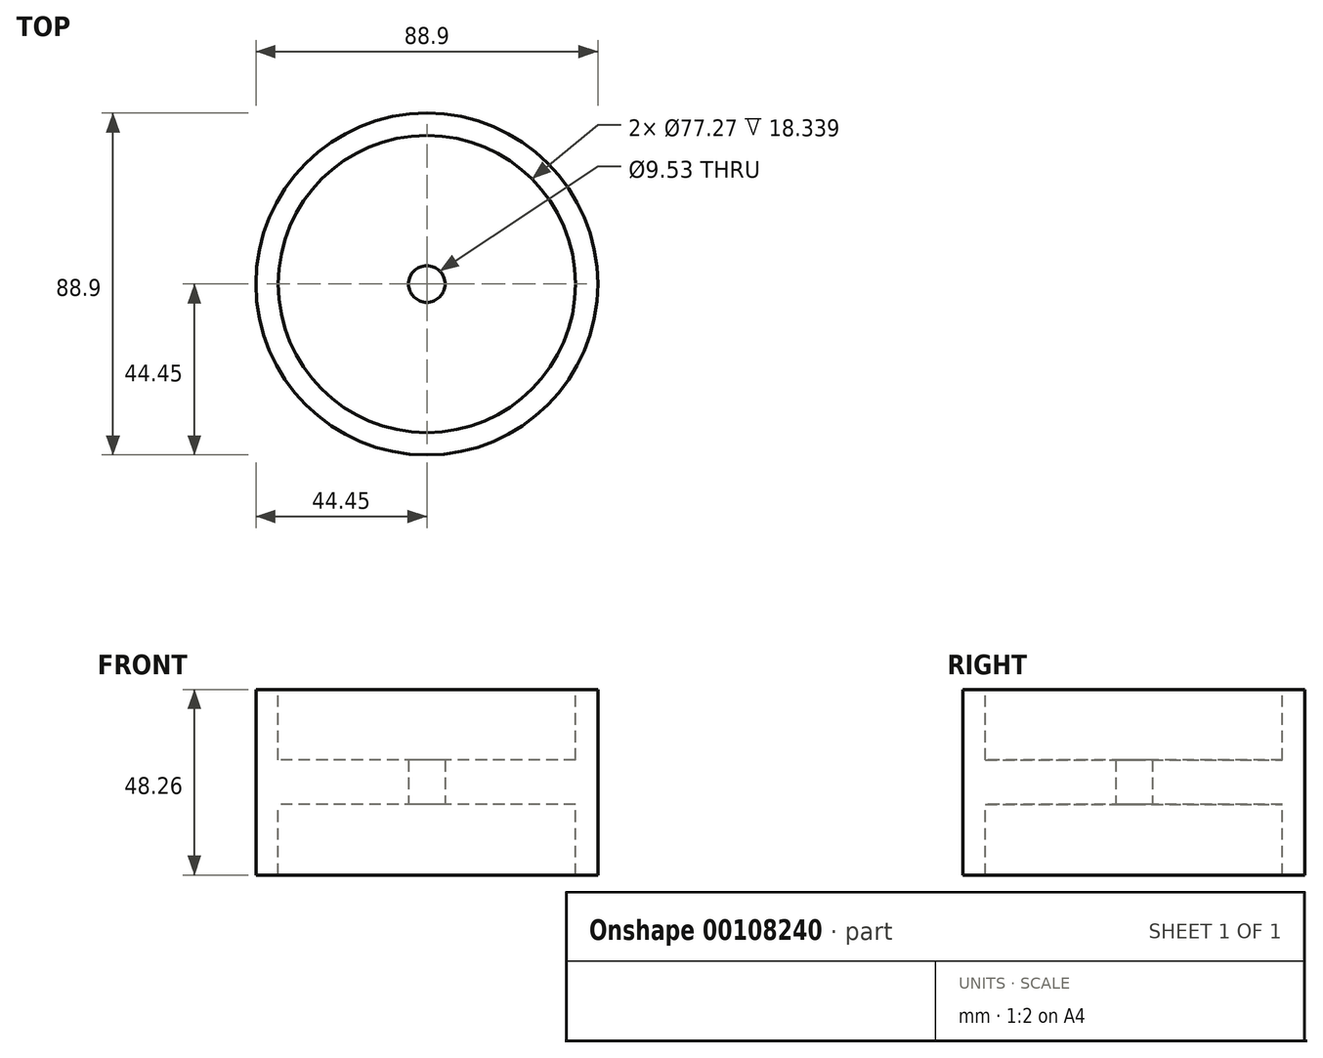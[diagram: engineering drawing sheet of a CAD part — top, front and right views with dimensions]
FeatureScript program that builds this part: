
annotation { "Feature Type Name" : "Feature", "Feature Type Description" : "" }
export const myFeature = defineFeature(function(context is Context, id is Id, definition is map)
    precondition{}
    {
        {
            var Q0;
            Q0=qCreatedBy(makeId("Front.planeOp"),FACE);
            var sketch = newSketch(context, id + "F0", { "sketchPlane" : qUnion([Q0])});
            skLineSegment(sketch, "E0", {"start": v(0, 190.5) * mm, "end": v(0, -190.5) * mm, "construction": true});
            skLineSegment(sketch, "E1", {"start": v(38.63, -24.13) * mm, "end": v(38.63, 24.13) * mm});
            skLineSegment(sketch, "E2", {"start": v(44.45, 24.13) * mm, "end": v(44.45, -24.13) * mm});
            skPoint(sketch, "E3", {"position": v(38.63, 0) * mm});
            skLineSegment(sketch, "E4", {"start": v(38.63, 24.13) * mm, "end": v(44.45, 24.13) * mm});
            skLineSegment(sketch, "E5", {"start": v(38.63, -24.13) * mm, "end": v(44.45, -24.13) * mm});
            skSolve(sketch);
        }
        {
            var Q0;
            Q0=makeQuery(id+"F0.imprint","IMPRINT",FACE,{"disambiguationData":[TD([[makeQuery(id+"F0.imprint","IMPRINT",EDGE,{"derivedFrom":sQuery(id+"F0.wireOp",EDGE,"E1")}),-1.0]])]});
            var Q1;
            Q1=sQuery(id+"F0.wireOp",EDGE,"E0");
            revolve(context, id + "F1", {"entities" : qUnion([Q0]), "axis" : qUnion([Q1]), "revolveType" : RevolveType.FULL});
        }
        {
            var Q0;
            Q0=qCreatedBy(makeId("Top.planeOp"),FACE);
            var sketch = newSketch(context, id + "F2", { "sketchPlane" : qUnion([Q0])});
            skCircle(sketch, "E6", {"center": v(0, 0) * mm, "radius": 38.63 * mm});
            skCircle(sketch, "E7", {"center": v(0, 0) * mm, "radius": 4.76 * mm});
            skSolve(sketch);
        }
        {
            var Q0;
            Q0=makeQuery(id+"F2.imprint","IMPRINT",FACE,{"disambiguationData":[TD([[makeQuery(id+"F2.imprint","IMPRINT",EDGE,{"derivedFrom":sQuery(id+"F2.wireOp",EDGE,"E6")}),1.0]])]});
            extrude(context, id + "F3", {"entities" : qUnion([Q0]), "operationType" : NewBodyOperationType.ADD, "endBound" : BoundingType.SYMMETRIC, "depth" : 11.58 * mm});
        }
    });
